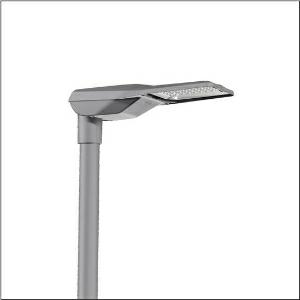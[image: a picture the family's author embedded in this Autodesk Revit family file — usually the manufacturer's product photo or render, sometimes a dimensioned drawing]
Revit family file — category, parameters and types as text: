
# Revit family: streetlight_sl_21_iq_mini___stw1_0a_5xe2e31d08gb_aef3
name_source: partatom
category: Lighting Fixtures
units: mm (PartAtom-declared; Revit-internal decimal feet)

## family parameters
Cut with Voids When Loaded = No
Host = Face
Light Source = No
Part Type = Normal
Room Calculation Point = No
Round Connector Dimension = Use Diameter
Shared = No

## types (1)
- --- (1 x LED, 5680 lm, 37.1 W, 3000K)
    Apparent Load = 37 VA
    CIE Flux Codes = 38 75 98 100 100
    Color Rendering = 70
    Color Temperature = 3000K
    Default Elevation = 1800 mm
    Description = Streetlight SL 21 iQ mini, mast luminaire, primary light control with lens, of PMMA, primary optical cover: cover, of toughened safety glass, transparent, light distribution: STW1.0a, light emission: direct distribution, primary light characteristic: asymmetric, installation type: post-top, side-entry, LED, High Power LED, rated luminous flux: 5.680lm, luminous efficacy: 153lm/W, light colour: 730, colour temperature: 3000K, control gear: iQ-Comfort, control: Auto-Match, Temp-Guard, Lumen-Switch, Night-Set, Smart-Wire, Light-Fading, Desk-Remote (wireless, voltage-free reading and setting of iQ features in the workshop via application-optimized NFC function/RFID function), optimised constant luminous flux control (CLO 2.0), pre-setting: linear dimming characteristic, mains connection: 220..240V, AC, 50/60Hz, start of lifetime: 37W, end of service life: 39W, reduction: 18W, luminaire housing, of diecast aluminium, powder-coated, Siteco® metallic grey (DB 702S), corrosivity category C5 mid according to DIN EN ISO 12944, please order mast flange separately, inclination adjustable: 0°, 5°, 10°, 15°, sealing non-destructively replaceable, multi-level sealing system, length: 628mm, width: 235mm, height: 110mm, mast flange for spigot size: 42mm (side-entry): 5XC10008XM4, 60/48mm (side-entry/post-top): 5XC10108XM2, 76/60mm (side-entry/post-top): 5XC10108XM1, mounting height: 4..8m, protection rating (complete): IP66, insulation class (complete): insulation class II (safety insulation), certification: CE, ENEC, ENEC+, VDE, impact resistance: IK10, permissible operating ambient temperature for outdoor applications: -40..+50°C, standard-compliant lighting for roads and squares, packaging unit: 1 piece

Light Distribution: STW1.0a
    Height = 110 mm
    Lamp = 1 x LED
    Lamp Light Flux = 5680 lm
    Lamp Power = 37.1 W
    Lamp count = 1
    Length = 625 mm
    Luminous efficacy = 153 lm/W
    Manufacturer = Siteco
    ModVariant = No
    Model = 5XE2E31D08GB
    Number of Poles = 1
    OnlyDefault = Yes
    Power Factor = 1
    Product Name = Streetlight SL 21 iQ mini | STW1.0a
    Product group = mast luminaire | pylon top
    ProductGroupID = 6100
    Protection Class = Protection class II
    Protection Degree = IP 66
    RLX_Detail_Level = 1
    RLX_Emergency_Light_Flux = 0 lm
    RLX_Emergency_Type = 0
    RLX_Emergency_Type_DB = No
    RlxData = <blob elided: 26361 chars, md5=332b9e4f>
    Socket = socket
    Standby Power = 0 W
    System Light Flux = 5680 lm
    System Power = 37 W
    Type Comments = factory setting: luminous flux: 100 % | dim-lin: 254 | 385 mA
    Type Image = l_1003519.jpg
    URL = http://relux.com
    VarID = @adj_208897
    Voltage = 0 V
    Weight = 0.00 kg
    Width = 234 mm

## geometry (parser evidence)
native form markers: Blend x4, Sweep x9
no freeform markers — native parametric forms only
